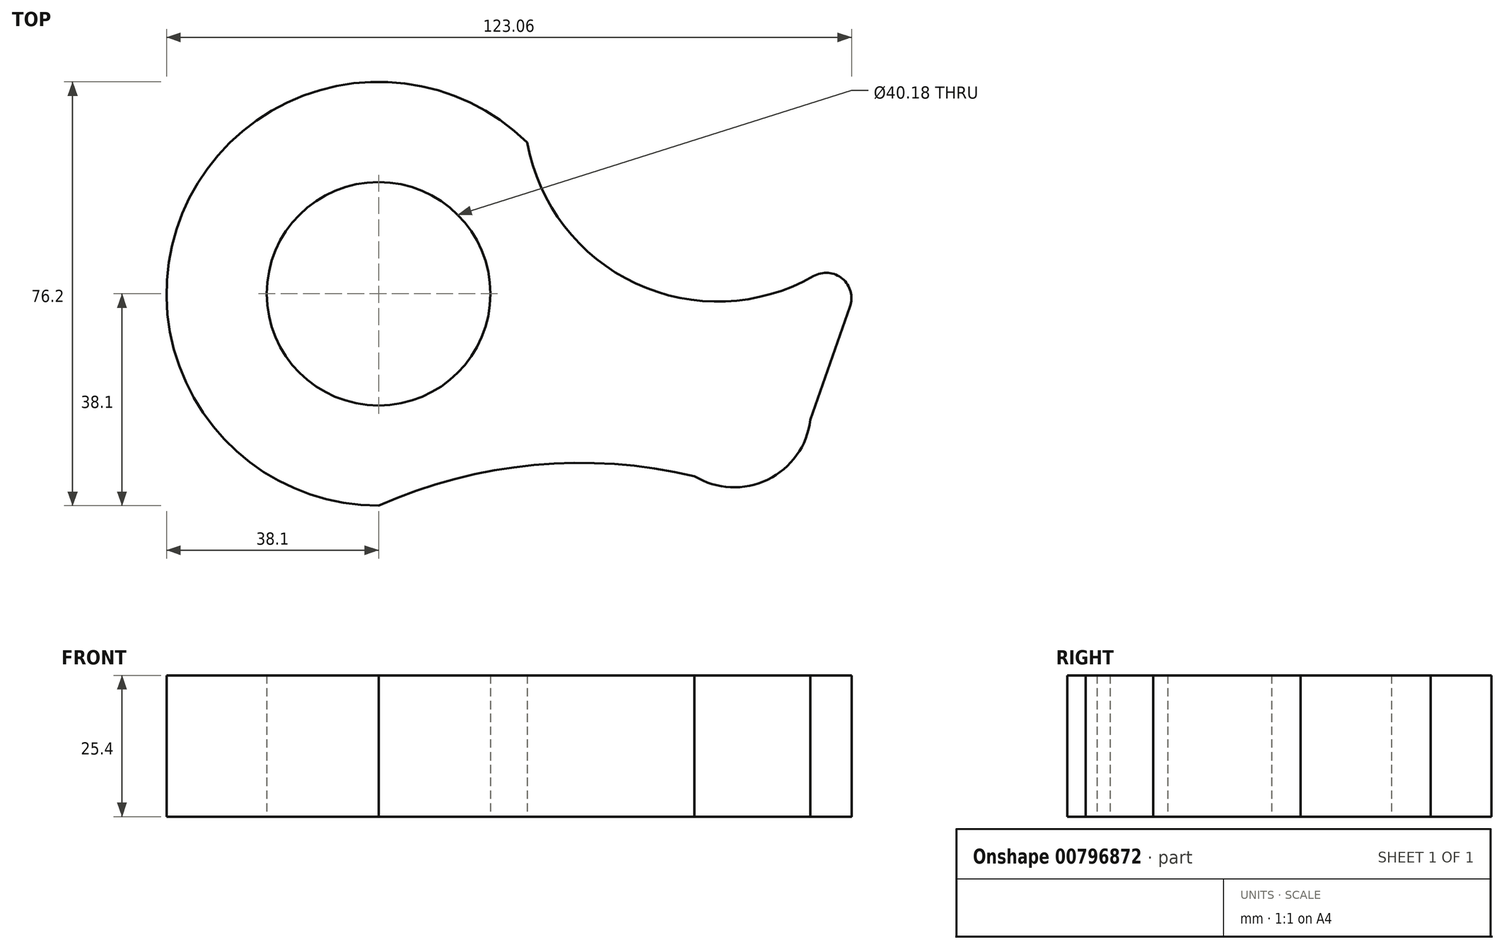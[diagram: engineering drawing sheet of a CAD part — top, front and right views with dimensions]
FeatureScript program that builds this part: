
annotation { "Feature Type Name" : "Feature", "Feature Type Description" : "" }
export const myFeature = defineFeature(function(context is Context, id is Id, definition is map)
    precondition{}
    {
        {
            var Q0;
            Q0=qCreatedBy(makeId("Top.planeOp"),FACE);
            var sketch = newSketch(context, id + "F0", { "sketchPlane" : qUnion([Q0])});
            skArc(sketch, "E0", {"start": v(26.71, 27.17) * mm, "mid": v(-35.26, 14.43) * mm, "end": v(0, -38.1) * mm});
            skCircle(sketch, "E1", {"center": v(0, 0) * mm, "radius": 20.1 * mm});
            skArc(sketch, "E2", {"start": v(56.71, -32.79) * mm, "mid": v(69.9, -33.42) * mm, "end": v(77.57, -22.68) * mm});
            skArc(sketch, "E3", {"start": v(63.89, -34.8) * mm, "mid": v(31.64, -30.52) * mm, "end": v(0, -38.1) * mm});
            skLineSegment(sketch, "E4", {"start": v(77.5, -22.86) * mm, "end": v(84.7, -2.32) * mm});
            skArc(sketch, "E5", {"start": v(26.71, 27.17) * mm, "mid": v(46.2, 1.85) * mm, "end": v(78.12, 3.16) * mm});
            skPoint(sketch, "E6.visualSharp", {"position": v(91.32, 16.57) * mm});
            skArc(sketch, "E6.filletArc", {"start": v(84.7, -2.32) * mm, "mid": v(83.31, 2.7) * mm, "end": v(78.12, 3.16) * mm});
            skSolve(sketch);
        }
        {
            var Q0;
            Q0 = qSketchRegion(id + "F0", true);
            extrude(context, id + "F1", {"entities" : qUnion([Q0]), "depth" : 25.4 * mm, "offsetDistance" : 25.4 * mm});
        }
    });
